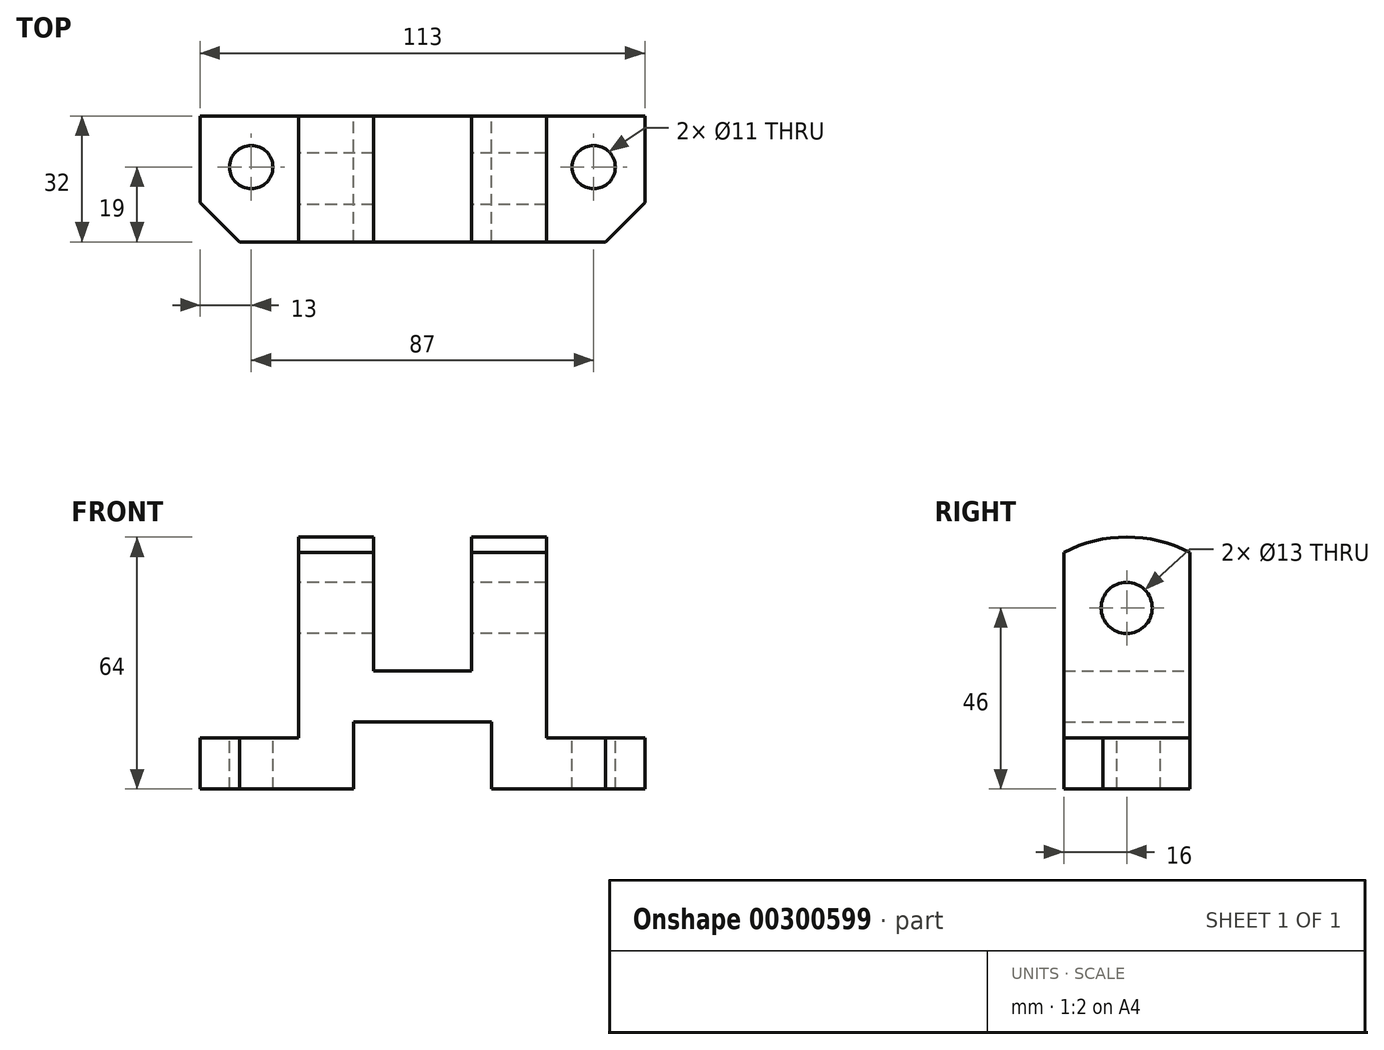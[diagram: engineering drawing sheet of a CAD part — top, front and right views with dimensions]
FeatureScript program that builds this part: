
annotation { "Feature Type Name" : "Feature", "Feature Type Description" : "" }
export const myFeature = defineFeature(function(context is Context, id is Id, definition is map)
    precondition{}
    {
        {
            var Q0;
            Q0=qCreatedBy(makeId("Right.planeOp"),FACE);
            var sketch = newSketch(context, id + "F0", { "sketchPlane" : qUnion([Q0])});
            skLineSegment(sketch, "E0", {"start": v(0, -92.87) * mm, "end": v(0, 120.95) * mm, "construction": true});
            skLineSegment(sketch, "E1", {"start": v(0, 0) * mm, "end": v(16, 0) * mm});
            skLineSegment(sketch, "E2", {"start": v(16, 0) * mm, "end": v(16, 60.13) * mm});
            skLineSegment(sketch, "E3.MirrorCS", {"start": v(0, 0) * mm, "end": v(-16, 0) * mm});
            skLineSegment(sketch, "E4.MirrorCS", {"start": v(-16, 0) * mm, "end": v(-16, 60.13) * mm});
            skArc(sketch, "E5", {"start": v(16, 60.13) * mm, "mid": v(8.23, 63.02) * mm, "end": v(0, 64) * mm});
            skArc(sketch, "E6.MirrorCS", {"start": v(-16, 60.13) * mm, "mid": v(-8.23, 63.02) * mm, "end": v(0, 64) * mm});
            skSolve(sketch);
        }
        {
            var Q0;
            Q0=makeQuery(id+"F0.imprint","IMPRINT",FACE,{"disambiguationData":[TD([[makeQuery(id+"F0.imprint","IMPRINT",EDGE,{"derivedFrom":sQuery(id+"F0.wireOp",EDGE,"E1")}),1.0]])]});
            extrude(context, id + "F1", {"entities" : qUnion([Q0]), "endBound" : BoundingType.SYMMETRIC, "depth" : 113 * mm});
        }
        {
            var Q0;
            Q0=makeQuery(id+"F1.opExtrude","CAP_FACE",FACE,{"disambiguationData":[OSD([sQuery(id+"F0.wireOp",EDGE,"E1"),sQuery(id+"F0.wireOp",EDGE,"E2"),sQuery(id+"F0.wireOp",EDGE,"E3.MirrorCS"),sQuery(id+"F0.wireOp",EDGE,"E4.MirrorCS"),sQuery(id+"F0.wireOp",EDGE,"E5"),sQuery(id+"F0.wireOp",EDGE,"E6.MirrorCS")])],"isStart":false});
            var sketch = newSketch(context, id + "F2", { "sketchPlane" : qUnion([Q0])});
            skArc(sketch, "E7", {"start": v(16, 60.13) * mm, "mid": v(0, 64) * mm, "end": v(-16, 60.13) * mm});
            skLineSegment(sketch, "E8", {"start": v(-16, 60.13) * mm, "end": v(-16, 13) * mm});
            skLineSegment(sketch, "E9", {"start": v(-16, 13) * mm, "end": v(16, 13) * mm});
            skLineSegment(sketch, "E10", {"start": v(16, 13) * mm, "end": v(16, 60.13) * mm});
            skSolve(sketch);
        }
        {
            var Q0;
            Q0 = qSketchRegion(id + "F2", true);
            extrude(context, id + "F3", {"entities" : qUnion([Q0]), "operationType" : NewBodyOperationType.REMOVE, "oppositeDirection" : true, "depth" : 25 * mm});
        }
        {
            var Q0;
            Q0=makeQuery(id+"F1.opExtrude","CAP_FACE",FACE,{"disambiguationData":[OSD([sQuery(id+"F0.wireOp",EDGE,"E1"),sQuery(id+"F0.wireOp",EDGE,"E2"),sQuery(id+"F0.wireOp",EDGE,"E3.MirrorCS"),sQuery(id+"F0.wireOp",EDGE,"E4.MirrorCS"),sQuery(id+"F0.wireOp",EDGE,"E5"),sQuery(id+"F0.wireOp",EDGE,"E6.MirrorCS")])],"isStart":true});
            var sketch = newSketch(context, id + "F4", { "sketchPlane" : qUnion([Q0])});
            skArc(sketch, "E11", {"start": v(16, 60.13) * mm, "mid": v(0, 64) * mm, "end": v(-16, 60.13) * mm});
            skLineSegment(sketch, "E12", {"start": v(-16, 60.13) * mm, "end": v(-16, 13) * mm});
            skLineSegment(sketch, "E13", {"start": v(-16, 13) * mm, "end": v(16, 13) * mm});
            skLineSegment(sketch, "E14", {"start": v(16, 13) * mm, "end": v(16, 60.13) * mm});
            skSolve(sketch);
        }
        {
            var Q0;
            Q0 = qSketchRegion(id + "F4", true);
            extrude(context, id + "F5", {"entities" : qUnion([Q0]), "operationType" : NewBodyOperationType.REMOVE, "oppositeDirection" : true, "depth" : 25 * mm});
        }
        {
            var Q0;
            Q0=qCreatedBy(makeId("Right.planeOp"),FACE);
            var sketch = newSketch(context, id + "F6", { "sketchPlane" : qUnion([Q0])});
            skLineSegment(sketch, "E15", {"start": v(-16, 30) * mm, "end": v(16, 30) * mm});
            skLineSegment(sketch, "E16", {"start": v(16, 30) * mm, "end": v(16, 60.13) * mm});
            skLineSegment(sketch, "E17", {"start": v(-16, 30) * mm, "end": v(-16, 60.13) * mm});
            skArc(sketch, "E18", {"start": v(16, 60.13) * mm, "mid": v(0, 64) * mm, "end": v(-16, 60.13) * mm});
            skSolve(sketch);
        }
        {
            var Q0;
            Q0 = qSketchRegion(id + "F6", true);
            extrude(context, id + "F7", {"entities" : qUnion([Q0]), "operationType" : NewBodyOperationType.REMOVE, "endBound" : BoundingType.SYMMETRIC, "oppositeDirection" : true, "depth" : 25 * mm});
        }
        {
            var Q0;
            Q0=qCreatedBy(makeId("Right.planeOp"),FACE);
            var sketch = newSketch(context, id + "F8", { "sketchPlane" : qUnion([Q0])});
            skLineSegment(sketch, "E19.bottom", {"start": v(-16, 0) * mm, "end": v(16, 0) * mm});
            skLineSegment(sketch, "E19.top", {"start": v(-16, 17) * mm, "end": v(16, 17) * mm});
            skLineSegment(sketch, "E19.left", {"start": v(-16, 0) * mm, "end": v(-16, 17) * mm});
            skLineSegment(sketch, "E19.right", {"start": v(16, 0) * mm, "end": v(16, 17) * mm});
            skSolve(sketch);
        }
        {
            var Q0;
            Q0 = qSketchRegion(id + "F8", true);
            extrude(context, id + "F9", {"entities" : qUnion([Q0]), "operationType" : NewBodyOperationType.REMOVE, "endBound" : BoundingType.SYMMETRIC, "oppositeDirection" : true, "depth" : 35 * mm});
        }
        {
            var Q0;
            Q0=qCreatedBy(makeId("Right.planeOp"),FACE);
            var sketch = newSketch(context, id + "F10", { "sketchPlane" : qUnion([Q0])});
            skCircle(sketch, "E20", {"center": v(0, 46) * mm, "radius": 6.5 * mm});
            skSolve(sketch);
        }
        {
            var Q0;
            Q0 = qSketchRegion(id + "F10", true);
            extrude(context, id + "F11", {"entities" : qUnion([Q0]), "operationType" : NewBodyOperationType.REMOVE, "endBound" : BoundingType.THROUGH_ALL, "depth" : 25 * mm, "hasSecondDirection" : true, "secondDirectionBound" : SecondDirectionBoundingType.THROUGH_ALL, "secondDirectionOppositeDirection" : true, "secondDirectionDepth" : 25 * mm});
        }
        {
            var Q0;
            Q0=makeQuery(id+"F5.boolean.opBoolean","COPY",FACE,{"derivedFrom":makeQuery(id+"F5.opExtrude","SWEPT_FACE",FACE,{"disambiguationData":[OSD([sQuery(id+"F4.wireOp",EDGE,"E13")])]})});
            var sketch = newSketch(context, id + "F12", { "sketchPlane" : qUnion([Q0])});
            skCircle(sketch, "E21", {"center": v(-43.5, 3) * mm, "radius": 5.5 * mm});
            skCircle(sketch, "E22", {"center": v(43.5, 3) * mm, "radius": 5.5 * mm});
            skSolve(sketch);
        }
        {
            var Q0;
            Q0 = qSketchRegion(id + "F12", true);
            extrude(context, id + "F13", {"entities" : qUnion([Q0]), "operationType" : NewBodyOperationType.REMOVE, "endBound" : BoundingType.THROUGH_ALL, "oppositeDirection" : true, "depth" : 25 * mm});
        }
        {
            var Q0;
            Q0=makeQuery(id+"F1.opExtrude","CAP_EDGE",EDGE,{"disambiguationData":[OSD([sQuery(id+"F0.wireOp",EDGE,"E4.MirrorCS")])],"isStart":false});
            var Q1;
            Q1=makeQuery(id+"F1.opExtrude","CAP_EDGE",EDGE,{"disambiguationData":[OSD([sQuery(id+"F0.wireOp",EDGE,"E4.MirrorCS")])],"isStart":true});
            chamfer(context, id + "F14", {"entities" : qUnion([Q0, Q1]), "chamferType" : ChamferType.OFFSET_ANGLE, "width" : 10 * mm, "oppositeDirection" : false, "angle" : 45 * degree, "tangentPropagation" : true});
        }
    });
